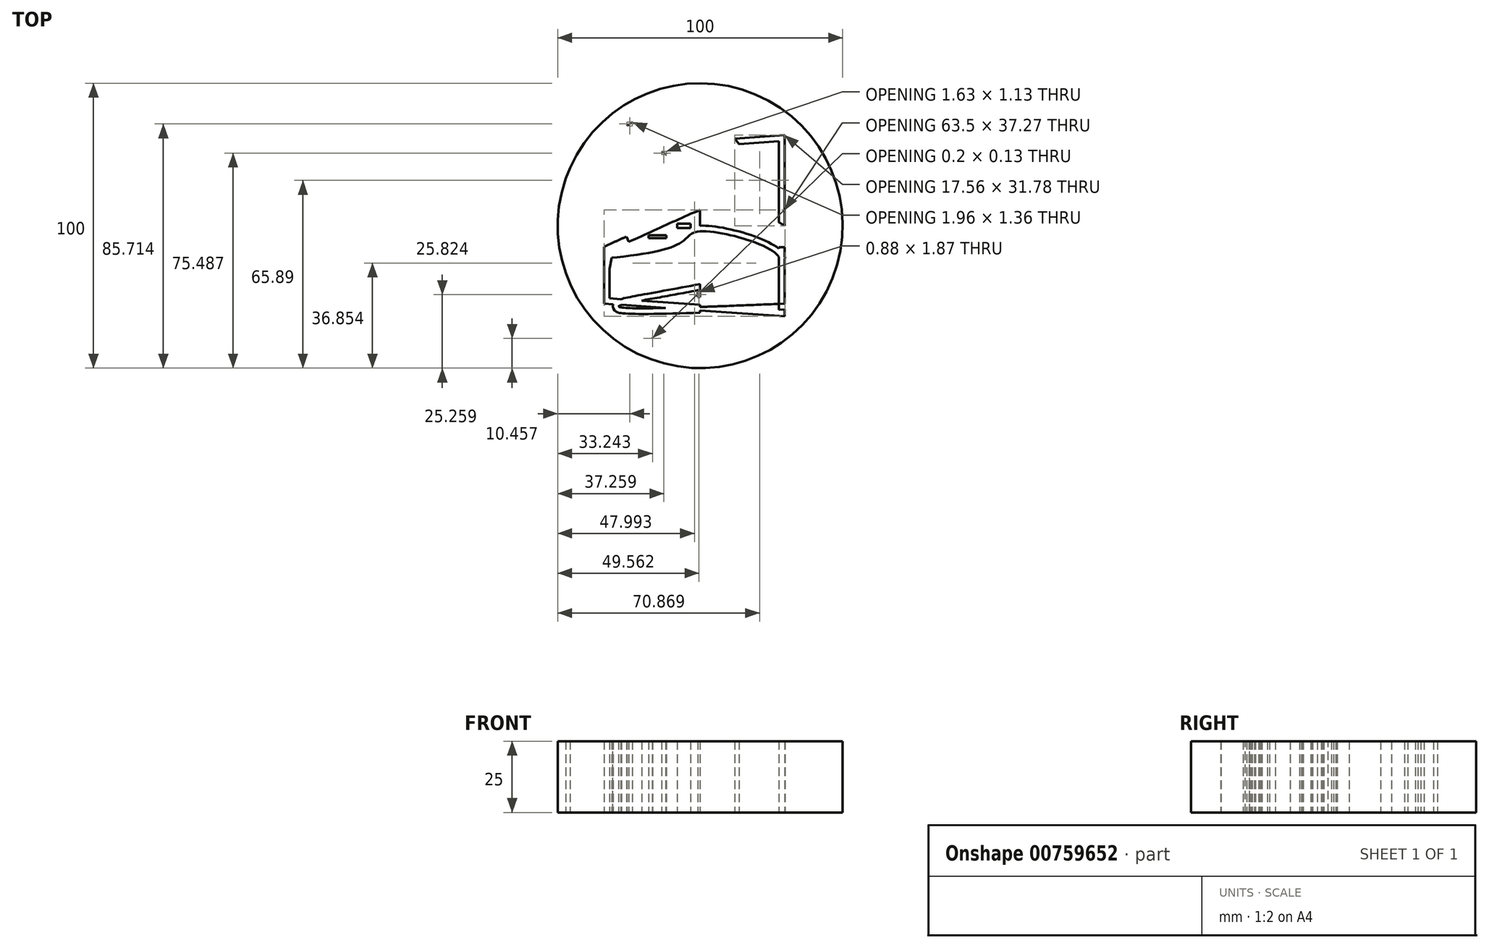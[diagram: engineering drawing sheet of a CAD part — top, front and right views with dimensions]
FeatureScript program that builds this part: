
annotation { "Feature Type Name" : "Feature", "Feature Type Description" : "" }
export const myFeature = defineFeature(function(context is Context, id is Id, definition is map)
    precondition{}
    {
        {
            var Q0;
            Q0=qCreatedBy(makeId("Top.planeOp"),FACE);
            var sketch = newSketch(context, id + "F0", { "sketchPlane" : qUnion([Q0])});
            skArc(sketch, "E0", {"start": v(33.76, -27.38) * mm, "mid": v(43.36, 3.01) * mm, "end": v(29.65, 31.78) * mm});
            skLineSegment(sketch, "E1", {"start": v(-33.76, 26.15) * mm, "end": v(-33.76, -27.38) * mm});
            skLineSegment(sketch, "E2", {"start": v(29.65, 31.78) * mm, "end": v(29.65, -3.54) * mm});
            skLineSegment(sketch, "E3", {"start": v(29.65, -27.38) * mm, "end": v(29.65, -31.78) * mm});
            skLineSegment(sketch, "E4", {"start": v(-29.02, 27.7) * mm, "end": v(-18.04, 28.47) * mm});
            skLineSegment(sketch, "E5", {"start": v(-33.76, -27.38) * mm, "end": v(29.65, -31.78) * mm});
            skLineSegment(sketch, "E6", {"start": v(0, 29.72) * mm, "end": v(0, -31.78) * mm});
            skArc(sketch, "E7", {"start": v(-9.95, 7.98) * mm, "mid": v(-7.68, 17.83) * mm, "end": v(-13.55, 26.05) * mm});
            skArc(sketch, "E8.0", {"start": v(-42.91, 16.74) * mm, "mid": v(-23.86, -39.18) * mm, "end": v(34.58, -30.54) * mm});
            skFitSpline(sketch, "E9.trimOffspring", {"points": [v(-33.76, -9.55) * mm, v(-8.04, -4.35) * mm, v(0, 0) * mm, v(29.65, -11.89) * mm, v(-27.62, -27.8) * mm, v(29.65, -27.38) * mm], "startDerivative": vector(179.63, 19.42) * mm, "endDerivative": vector(370.43, 15.15) * mm});
            skLineSegment(sketch, "E10.bottom", {"start": v(14.73, -23.24) * mm, "end": v(-0.88, -23.24) * mm});
            skLineSegment(sketch, "E10.top", {"start": v(14.73, -25.11) * mm, "end": v(-0.88, -25.11) * mm});
            skLineSegment(sketch, "E10.left", {"start": v(14.73, -23.24) * mm, "end": v(14.73, -25.11) * mm});
            skLineSegment(sketch, "E10.right", {"start": v(-0.88, -23.24) * mm, "end": v(-0.88, -25.11) * mm});
            skPoint(sketch, "E10.middle", {"position": v(6.93, -24.18) * mm});
            skLineSegment(sketch, "E11.bottom", {"start": v(27.65, -23.66) * mm, "end": v(20.84, -23.66) * mm});
            skLineSegment(sketch, "E11.top", {"start": v(27.65, -21.37) * mm, "end": v(20.84, -21.37) * mm});
            skLineSegment(sketch, "E11.left", {"start": v(29.65, -23.66) * mm, "end": v(29.65, -21.37) * mm});
            skLineSegment(sketch, "E11.right", {"start": v(20.84, -23.66) * mm, "end": v(20.84, -21.37) * mm});
            skPoint(sketch, "E11.middle", {"position": v(25.25, -22.51) * mm});
            skLineSegment(sketch, "E12.bottom", {"start": v(-11.85, -4.36) * mm, "end": v(-18.03, -4.36) * mm});
            skLineSegment(sketch, "E12.top", {"start": v(-11.85, -3.37) * mm, "end": v(-18.03, -3.37) * mm});
            skLineSegment(sketch, "E12.left", {"start": v(-11.85, -4.36) * mm, "end": v(-11.85, -3.37) * mm});
            skLineSegment(sketch, "E12.right", {"start": v(-18.03, -4.36) * mm, "end": v(-18.03, -3.37) * mm});
            skPoint(sketch, "E12.middle", {"position": v(-14.94, -3.87) * mm});
            skLineSegment(sketch, "E13.bottom", {"start": v(-3.33, -0.76) * mm, "end": v(-8.09, -0.76) * mm});
            skLineSegment(sketch, "E13.top", {"start": v(-3.33, 0.76) * mm, "end": v(-8.09, 0.76) * mm});
            skLineSegment(sketch, "E13.left", {"start": v(-3.33, -0.76) * mm, "end": v(-3.33, 0.76) * mm});
            skLineSegment(sketch, "E13.right", {"start": v(-8.09, -0.76) * mm, "end": v(-8.09, 0.76) * mm});
            skPoint(sketch, "E13.middle", {"position": v(-5.7, 0) * mm});
            skLineSegment(sketch, "E14.bottom", {"start": v(17.1, 2.32) * mm, "end": v(3, 2.32) * mm});
            skLineSegment(sketch, "E14.top", {"start": v(17.1, 4.3) * mm, "end": v(3, 4.3) * mm});
            skLineSegment(sketch, "E14.left", {"start": v(17.1, 2.32) * mm, "end": v(17.1, 4.3) * mm});
            skLineSegment(sketch, "E14.right", {"start": v(3, 2.32) * mm, "end": v(3, 4.3) * mm});
            skPoint(sketch, "E14.middle", {"position": v(10.04, 3.3) * mm});
            skLineSegment(sketch, "E15.left", {"start": v(29.65, -3.37) * mm, "end": v(29.65, -1.9) * mm});
            skPoint(sketch, "E15.middle", {"position": v(25.25, -2.64) * mm});
            skLineSegment(sketch, "E16.0", {"start": v(-28.89, 25.71) * mm, "end": v(-26.2, 25.9) * mm});
            skArc(sketch, "E17", {"start": v(-47.2, 16.53) * mm, "mid": v(46.48, -18.43) * mm, "end": v(-45.7, 20.3) * mm});
            skLineSegment(sketch, "E18.0", {"start": v(-31.76, 18.09) * mm, "end": v(-31.76, 13.5) * mm});
            skLineSegment(sketch, "E19.0", {"start": v(-31.76, -25.51) * mm, "end": v(27.65, -29.64) * mm});
            skLineSegment(sketch, "E20.0", {"start": v(27.65, 31.78) * mm, "end": v(27.65, 31.64) * mm});
            skArc(sketch, "E21.trimOffspring", {"start": v(37.17, -27.38) * mm, "mid": v(24.36, 39.52) * mm, "end": v(-41.13, 20.79) * mm});
            skLineSegment(sketch, "E22.trimOffspring", {"start": v(29.65, -7.53) * mm, "end": v(29.65, -27.38) * mm});
            skLineSegment(sketch, "E23.trimOffspring", {"start": v(27.65, -7.53) * mm, "end": v(27.65, -27.38) * mm});
            skLineSegment(sketch, "E24.left", {"start": v(-27.84, -8.9) * mm, "end": v(-27.84, -8.9) * mm});
            skFitSpline(sketch, "E25.trimOffspring", {"points": [v(-33.76, -9.55) * mm, v(-9.87, 1.2) * mm, v(11.16, 7.64) * mm, v(29.65, 0) * mm], "startDerivative": vector(67.01, 29.77) * mm, "endDerivative": vector(57.9, -35.17) * mm});
            skFitSpline(sketch, "E26.trimOffspring", {"points": [v(-33.76, -9.55) * mm, v(-8.04, -4.35) * mm, v(0, 0) * mm, v(29.65, -11.89) * mm, v(-27.62, -27.8) * mm, v(29.65, -27.38) * mm], "startDerivative": vector(179.63, 19.42) * mm, "endDerivative": vector(370.43, 15.15) * mm});
            skArc(sketch, "E27.0", {"start": v(-11.54, 9.19) * mm, "mid": v(-27.29, 22.44) * mm, "end": v(-12.93, 7.7) * mm});
            skLineSegment(sketch, "E28", {"start": v(23.18, 36.76) * mm, "end": v(27.65, 31.78) * mm});
            skLineSegment(sketch, "E29", {"start": v(-18.04, 28.47) * mm, "end": v(-23.17, 35.57) * mm});
            skLineSegment(sketch, "E30", {"start": v(-16.66, -39.48) * mm, "end": v(0, -31.78) * mm});
            skLineSegment(sketch, "E31", {"start": v(0, -31.78) * mm, "end": v(10.47, -33.17) * mm});
            skLineSegment(sketch, "E32", {"start": v(10.47, -33.17) * mm, "end": v(29.65, -31.78) * mm});
            skLineSegment(sketch, "E33", {"start": v(29.65, 28.51) * mm, "end": v(41.96, 1.31) * mm});
            skLineSegment(sketch, "E34", {"start": v(43.42, -1.9) * mm, "end": v(38.27, -11.44) * mm});
            skLineSegment(sketch, "E35", {"start": v(-33.76, 26.15) * mm, "end": v(-31.76, 13.5) * mm});
            skLineSegment(sketch, "E36", {"start": v(-31.76, -15.21) * mm, "end": v(-29.32, -1.9) * mm});
            skLineSegment(sketch, "E37.top", {"start": v(35.24, -15.12) * mm, "end": v(36.28, -15.12) * mm});
            skLineSegment(sketch, "E38.trimOffspring", {"start": v(36.28, -15.12) * mm, "end": v(29.65, -27.38) * mm});
            skLineSegment(sketch, "E39.0", {"start": v(29.65, 32.22) * mm, "end": v(29.65, -3.54) * mm});
            skLineSegment(sketch, "E39.2", {"start": v(22.96, 36.9) * mm, "end": v(23.03, 36.96) * mm});
            skLineSegment(sketch, "E39.6", {"start": v(-16.86, -39.6) * mm, "end": v(-1.76, -33.56) * mm});
            skLineSegment(sketch, "E40.0", {"start": v(10.61, -35.17) * mm, "end": v(27.11, -33.97) * mm});
            skLineSegment(sketch, "E41.0", {"start": v(30.93, 30.54) * mm, "end": v(43.35, 3.1) * mm});
            skLineSegment(sketch, "E42", {"start": v(-12.93, 7.7) * mm, "end": v(-11.61, 6.2) * mm});
            skLineSegment(sketch, "E43", {"start": v(-11.54, 9.19) * mm, "end": v(-9.95, 7.98) * mm});
            skLineSegment(sketch, "E44", {"start": v(33.76, -27.38) * mm, "end": v(37.17, -27.38) * mm});
            skLineSegment(sketch, "E45", {"start": v(31.85, -29.57) * mm, "end": v(34.58, -30.54) * mm});
            skPoint(sketch, "E46.orphan", {"position": v(-16.66, 26.56) * mm});
            skLineSegment(sketch, "E47.trimOffspring", {"start": v(-13.3, 28.8) * mm, "end": v(-11.92, 28.9) * mm});
            skPoint(sketch, "E48.orphan", {"position": v(28.88, 29.72) * mm});
            skArc(sketch, "E49.trimOffspring", {"start": v(22.96, 36.9) * mm, "mid": v(-1.67, 43.43) * mm, "end": v(-25.72, 35.03) * mm});
            skLineSegment(sketch, "E50", {"start": v(-47.2, 16.53) * mm, "end": v(-45.7, 20.3) * mm});
            skLineSegment(sketch, "E51.trimOffspring", {"start": v(27.65, -1.9) * mm, "end": v(20.85, -1.9) * mm});
            skFitSpline(sketch, "E52.0", {"points": [v(-34.57, -7.72) * mm, v(-31.78, -6.48) * mm, v(-27.59, -4.62) * mm, v(-22.03, -2.13) * mm, v(-17.87, -0.26) * mm, v(-14.42, 1.31) * mm, v(-11.67, 2.57) * mm, v(-8.93, 3.84) * mm, v(-5.5, 5.43) * mm, v(-1.34, 7.18) * mm, v(2.14, 8.37) * mm, v(4.94, 9.07) * mm, v(7.05, 9.45) * mm, v(8.82, 9.63) * mm, v(10.23, 9.67) * mm, v(11.65, 9.63) * mm, v(13.41, 9.46) * mm, v(15.47, 9.05) * mm, v(17.49, 8.47) * mm, v(20.12, 7.5) * mm, v(23.32, 6) * mm, v(27.05, 3.92) * mm, v(29.48, 2.44) * mm, v(30.69, 1.7) * mm]});
            skFitSpline(sketch, "E53.0", {"points": [v(-33.54, -11.54) * mm, v(-31.67, -11.33) * mm, v(-27.92, -10.93) * mm, v(-22.46, -10.26) * mm, v(-18.2, -9.6) * mm, v(-15.07, -8.96) * mm, v(-12.87, -8.43) * mm, v(-10.84, -7.82) * mm, v(-9.3, -7.24) * mm, v(-8.18, -6.72) * mm, v(-7.38, -6.3) * mm, v(-6.63, -5.82) * mm, v(-5.97, -5.34) * mm, v(-5.4, -4.86) * mm, v(-4.71, -4.25) * mm, v(-3.99, -3.58) * mm, v(-3.22, -2.96) * mm, v(-2.43, -2.51) * mm, v(-1.56, -2.22) * mm, v(-0.62, -2.05) * mm, v(0.5, -1.95) * mm, v(2.33, -1.98) * mm, v(5, -2.25) * mm, v(8.01, -2.74) * mm, v(11.2, -3.44) * mm, v(14.46, -4.3) * mm, v(17.64, -5.32) * mm, v(20.62, -6.44) * mm, v(23.28, -7.65) * mm, v(25.1, -8.68) * mm, v(26.23, -9.48) * mm, v(26.91, -10.05) * mm, v(27.39, -10.56) * mm, v(27.66, -10.97) * mm, v(27.74, -11.2) * mm, v(27.74, -11.26) * mm, v(27.74, -11.29) * mm, v(27.73, -11.32) * mm, v(27.69, -11.41) * mm, v(27.57, -11.6) * mm, v(27.27, -11.94) * mm, v(26.66, -12.44) * mm, v(25.8, -13) * mm, v(24.39, -13.76) * mm, v(22.13, -14.74) * mm, v(18.8, -15.9) * mm, v(14.98, -17.02) * mm, v(10.8, -18.1) * mm, v(6.34, -19.13) * mm, v(1.74, -20.1) * mm, v(-2.9, -21.03) * mm, v(-7.48, -21.9) * mm, v(-11.9, -22.7) * mm, v(-16.02, -23.44) * mm, v(-19.15, -24) * mm, v(-21.41, -24.41) * mm, v(-22.98, -24.7) * mm, v(-24.4, -24.99) * mm, v(-25.66, -25.25) * mm, v(-26.58, -25.46) * mm, v(-27.23, -25.62) * mm, v(-27.68, -25.73) * mm, v(-28.09, -25.85) * mm, v(-28.46, -25.97) * mm, v(-28.81, -26.1) * mm, v(-29.14, -26.24) * mm, v(-29.44, -26.4) * mm, v(-29.7, -26.58) * mm, v(-29.93, -26.78) * mm, v(-30.19, -27.06) * mm, v(-30.45, -27.5) * mm, v(-30.6, -28.03) * mm, v(-30.6, -28.52) * mm, v(-30.52, -28.99) * mm, v(-30.28, -29.49) * mm, v(-29.96, -29.87) * mm, v(-29.66, -30.1) * mm, v(-29.41, -30.26) * mm, v(-29.2, -30.36) * mm, v(-28.94, -30.46) * mm, v(-28.65, -30.54) * mm, v(-28.31, -30.62) * mm, v(-27.96, -30.68) * mm, v(-27.6, -30.73) * mm, v(-27.2, -30.77) * mm, v(-26.76, -30.81) * mm, v(-26.14, -30.86) * mm, v(-25.28, -30.9) * mm, v(-24.11, -30.94) * mm, v(-22.8, -30.97) * mm, v(-21.35, -30.99) * mm, v(-19.25, -30.99) * mm, v(-16.32, -30.96) * mm, v(-12.34, -30.89) * mm, v(-7.97, -30.78) * mm, v(-3.24, -30.64) * mm, v(1.8, -30.47) * mm, v(8.84, -30.21) * mm, v(18.15, -29.85) * mm, v(25.87, -29.53) * mm, v(29.73, -29.38) * mm]});
            skLineSegment(sketch, "E54", {"start": v(27.65, -27.38) * mm, "end": v(27.65, -29.58) * mm});
            skPoint(sketch, "E54.endSnap0", {"position": v(29.65, -29.58) * mm});
            skLineSegment(sketch, "E55", {"start": v(27.65, -29.58) * mm, "end": v(27.65, -29.64) * mm});
            skLineSegment(sketch, "E56.0", {"start": v(41.66, -0.96) * mm, "end": v(36.47, -10.55) * mm});
            skLineSegment(sketch, "E57", {"start": v(41.66, -0.96) * mm, "end": v(41.96, 1.31) * mm});
            skLineSegment(sketch, "E58", {"start": v(-33.62, -25.38) * mm, "end": v(-33.76, -25.38) * mm});
            skArc(sketch, "E59.trimOffspring", {"start": v(-32.8, -28.5) * mm, "mid": v(-0.71, -43.46) * mm, "end": v(31.85, -29.57) * mm});
            skLineSegment(sketch, "E60", {"start": v(36.47, -10.55) * mm, "end": v(38.27, -11.44) * mm});
            skLineSegment(sketch, "E61", {"start": v(29.65, -22.51) * mm, "end": v(35.24, -15.12) * mm});
            skLineSegment(sketch, "E62", {"start": v(-25.9, -3.86) * mm, "end": v(-25.08, -5.69) * mm});
            skLineSegment(sketch, "E63", {"start": v(-23.2, -8.4) * mm, "end": v(-23.33, -10.35) * mm});
            skLineSegment(sketch, "E64.0", {"start": v(-15.8, 30.44) * mm, "end": v(-14.4, 32.3) * mm});
            skLineSegment(sketch, "E65.0", {"start": v(-3.37, 43.33) * mm, "end": v(11.04, 33.3) * mm});
            skLineSegment(sketch, "E66.0", {"start": v(-16.38, 30.85) * mm, "end": v(-23.17, 35.57) * mm});
            skArc(sketch, "E67.trimOffspring", {"start": v(-23.76, 36.4) * mm, "mid": v(-32.37, 29) * mm, "end": v(-38.77, 19.65) * mm});
            skLineSegment(sketch, "E68", {"start": v(-23.76, 36.4) * mm, "end": v(-25.72, 35.03) * mm});
            skLineSegment(sketch, "E69", {"start": v(-16.38, 30.85) * mm, "end": v(-15.8, 30.44) * mm});
            skPoint(sketch, "E70.end.orphan", {"position": v(-16.57, 28.62) * mm});
            skLineSegment(sketch, "E71.0", {"start": v(-13.3, 28.8) * mm, "end": v(-3.89, 41.25) * mm});
            skPoint(sketch, "E72.end.orphan", {"position": v(14.63, 30.82) * mm});
            skPoint(sketch, "E73.start.orphan", {"position": v(15.8, 30.82) * mm});
            skLineSegment(sketch, "E74.trimOffspring", {"start": v(27.65, 29.64) * mm, "end": v(27.65, -1.9) * mm});
            skArc(sketch, "E75.trimOffspring", {"start": v(-31.47, 11.7) * mm, "mid": v(-23.03, 3.57) * mm, "end": v(-11.61, 6.2) * mm});
            skLineSegment(sketch, "E76.trimOffspring", {"start": v(-24.05, 36.19) * mm, "end": v(-24.06, 36.2) * mm});
            skFitSpline(sketch, "E77.trimOffspring", {"points": [v(-34.57, -7.72) * mm, v(-31.78, -6.48) * mm, v(-27.59, -4.62) * mm, v(-22.03, -2.13) * mm, v(-17.87, -0.26) * mm, v(-14.42, 1.31) * mm, v(-11.67, 2.57) * mm, v(-8.93, 3.84) * mm, v(-5.5, 5.43) * mm, v(-1.34, 7.18) * mm, v(2.14, 8.37) * mm, v(4.94, 9.07) * mm, v(7.05, 9.45) * mm, v(8.82, 9.63) * mm, v(10.23, 9.67) * mm, v(11.65, 9.63) * mm, v(13.41, 9.46) * mm, v(15.47, 9.05) * mm, v(17.49, 8.47) * mm, v(20.12, 7.5) * mm, v(23.32, 6) * mm, v(27.05, 3.92) * mm, v(29.48, 2.44) * mm, v(30.69, 1.7) * mm]});
            skLineSegment(sketch, "E78", {"start": v(12.09, 30.56) * mm, "end": v(29.65, 31.78) * mm});
            skLineSegment(sketch, "E79", {"start": v(13.65, 28.66) * mm, "end": v(27.65, 29.64) * mm});
            skLineSegment(sketch, "E80", {"start": v(10.57, 30.46) * mm, "end": v(11.46, 28.51) * mm});
            skLineSegment(sketch, "E81", {"start": v(12.09, 30.56) * mm, "end": v(13.65, 28.66) * mm});
            skFitSpline(sketch, "E82", {"points": [v(7.45, 25.37) * mm, v(13.65, 21.57) * mm, v(9.2, 15.55) * mm, v(17.63, 20.1) * mm, v(7.45, 25.37) * mm]});
            skLineSegment(sketch, "E83", {"start": v(-28.89, 25.71) * mm, "end": v(-29.02, 27.7) * mm});
            skArc(sketch, "E84.trimOffspring", {"start": v(-26.2, 25.9) * mm, "mid": v(-29.77, 22.56) * mm, "end": v(-31.76, 18.09) * mm});
            skLineSegment(sketch, "E85.trimOffspring", {"start": v(-14.8, 26.69) * mm, "end": v(-14.5, 26.71) * mm});
            skLineSegment(sketch, "E86.0", {"start": v(-14.5, 26.71) * mm, "end": v(-11.93, 24.92) * mm});
            skLineSegment(sketch, "E87", {"start": v(-3.89, 41.25) * mm, "end": v(6.76, 33.3) * mm});
            skPoint(sketch, "E88.center.orphan", {"position": v(10.96, 29.72) * mm});
            skLineSegment(sketch, "E89.trimOffspring", {"start": v(-1.76, -33.56) * mm, "end": v(10.2, -35.15) * mm});
            skLineSegment(sketch, "E90.trimOffspring", {"start": v(-11, 26.95) * mm, "end": v(11.46, 28.51) * mm});
            skLineSegment(sketch, "E91", {"start": v(-26.2, 25.9) * mm, "end": v(-14.8, 26.69) * mm});
            skPoint(sketch, "E92.orphan", {"position": v(-15.93, 28.62) * mm});
            skLineSegment(sketch, "E93.trimOffspring", {"start": v(-31.76, -15.21) * mm, "end": v(-31.76, -25.51) * mm});
            skLineSegment(sketch, "E94.trimOffspring", {"start": v(-31.47, 11.7) * mm, "end": v(-29.32, -1.9) * mm});
            skLineSegment(sketch, "E95", {"start": v(10.61, -35.17) * mm, "end": v(10.2, -35.15) * mm});
            skLineSegment(sketch, "E96", {"start": v(-16.66, -39.48) * mm, "end": v(-16.86, -39.6) * mm});
            skFitSpline(sketch, "E97.trimOffspring", {"points": [v(-33.76, -9.55) * mm, v(-8.04, -4.35) * mm, v(0, 0) * mm, v(29.65, -11.89) * mm, v(-27.62, -27.8) * mm, v(29.65, -27.38) * mm], "startDerivative": vector(179.63, 19.42) * mm, "endDerivative": vector(370.43, 15.15) * mm});
            skLineSegment(sketch, "E98", {"start": v(-16.66, -39.48) * mm, "end": v(-17.24, -39.9) * mm});
            skLineSegment(sketch, "E99", {"start": v(-41.13, 15.86) * mm, "end": v(-42.91, 16.74) * mm});
            skLineSegment(sketch, "E100", {"start": v(-41.13, 15.86) * mm, "end": v(-40.59, 15.55) * mm});
            skPoint(sketch, "E15.bottom.end.orphan", {"position": v(20.85, -3.37) * mm});
            skLineSegment(sketch, "E101", {"start": v(20.85, -1.9) * mm, "end": v(20.85, -2.92) * mm});
            skLineSegment(sketch, "E102", {"start": v(20.85, -2.92) * mm, "end": v(27.65, -2.92) * mm});
            skLineSegment(sketch, "E103.trimOffspring", {"start": v(27.65, -2.92) * mm, "end": v(27.65, -3.54) * mm});
            skLineSegment(sketch, "E104.top", {"start": v(27.65, -7.53) * mm, "end": v(29.65, -7.53) * mm});
            skLineSegment(sketch, "E105.bottom", {"start": v(27.65, -3.54) * mm, "end": v(29.65, -3.54) * mm});
            skLineSegment(sketch, "E106.trimOffspring", {"start": v(29.65, -4.5) * mm, "end": v(29.65, -4.5) * mm});
            skLineSegment(sketch, "E107.left", {"start": v(-17.39, 26.5) * mm, "end": v(-17.39, 26.2) * mm});
            skLineSegment(sketch, "E107.right", {"start": v(-11.92, 29.25) * mm, "end": v(-11.92, 28.9) * mm});
            skLineSegment(sketch, "E108.trimOffspring", {"start": v(0, 29.72) * mm, "end": v(10.57, 30.46) * mm});
            skLineSegment(sketch, "E109.left", {"start": v(6.56, 32.45) * mm, "end": v(6.56, 32.45) * mm});
            skLineSegment(sketch, "E109.right", {"start": v(7.46, 32.45) * mm, "end": v(7.46, 32.45) * mm});
            skLineSegment(sketch, "E110.bottom", {"start": v(6.76, 33.3) * mm, "end": v(11.04, 33.3) * mm});
            skPoint(sketch, "E111.start.orphan", {"position": v(-45.3, 15.86) * mm});
            skLineSegment(sketch, "E112", {"start": v(-41.13, 20.79) * mm, "end": v(-38.9, 19.72) * mm});
            skArc(sketch, "E113.trimOffspring", {"start": v(-40.59, 15.55) * mm, "mid": v(-42.92, -6.83) * mm, "end": v(-33.76, -27.38) * mm});
            skLineSegment(sketch, "E114", {"start": v(-38.9, 19.72) * mm, "end": v(-38.77, 19.65) * mm});
            skLineSegment(sketch, "E115.trimOffspring", {"start": v(-13.41, 33.6) * mm, "end": v(-6.3, 43) * mm});
            skLineSegment(sketch, "E116", {"start": v(-31.76, 13.5) * mm, "end": v(-31.43, 11.46) * mm});
            skLineSegment(sketch, "E117.trimOffspring", {"start": v(-13.3, 28.8) * mm, "end": v(-4.32, 29.42) * mm});
            skSolve(sketch);
        }
        {
            var Q0;
            {var subQ5=sQuery(id+"F0.wireOp",EDGE,"E18.0");Q0=makeQuery(id+"F0.imprint","IMPRINT",FACE,{"disambiguationData":[TD([[makeQuery(id+"F0.imprint","IMPRINT",EDGE,{"derivedFrom":subQ5}),1.0]])]});}
            var Q1;
            {var subQ9=sQuery(id+"F0.wireOp",EDGE,"E35");Q1=makeQuery(id+"F0.imprint","IMPRINT",FACE,{"disambiguationData":[TD([[makeQuery(id+"F0.imprint","IMPRINT",EDGE,{"derivedFrom":subQ9}),-1.0]])]});}
            var Q2;
            Q2=makeQuery(id+"F0.imprint","IMPRINT",FACE,{"disambiguationData":[TD([[makeQuery(id+"F0.imprint","IMPRINT",EDGE,{"derivedFrom":sQuery(id+"F0.wireOp",EDGE,"E8.0")}),1.0]])]});
            var Q3;
            {var subQ6=sQuery(id+"F0.wireOp",EDGE,"E40.0");Q3=makeQuery(id+"F0.imprint","IMPRINT",FACE,{"disambiguationData":[TD([[makeQuery(id+"F0.imprint","IMPRINT",EDGE,{"derivedFrom":subQ6}),-1.0]])]});}
            var Q4;
            {var subQ4=sQuery(id+"F0.wireOp",EDGE,"E31");Q4=makeQuery(id+"F0.imprint","IMPRINT",FACE,{"disambiguationData":[TD([[makeQuery(id+"F0.imprint","IMPRINT",EDGE,{"derivedFrom":subQ4}),1.0]])]});}
            var Q5;
            {var subQ7=sQuery(id+"F0.wireOp",EDGE,"E30");Q5=makeQuery(id+"F0.imprint","IMPRINT",FACE,{"disambiguationData":[TD([[makeQuery(id+"F0.imprint","IMPRINT",EDGE,{"derivedFrom":subQ7}),-1.0]])]});}
            var Q6;
            {var subQ6=sQuery(id+"F0.wireOp",EDGE,"E10.left");Q6=makeQuery(id+"F0.imprint","IMPRINT",FACE,{"disambiguationData":[TD([[makeQuery(id+"F0.imprint","IMPRINT",EDGE,{"derivedFrom":subQ6}),1.0]])]});}
            var Q7;
            {var subQ5=sQuery(id+"F0.wireOp",EDGE,"E10.left");Q7=makeQuery(id+"F0.imprint","IMPRINT",FACE,{"disambiguationData":[TD([[makeQuery(id+"F0.imprint","IMPRINT",EDGE,{"derivedFrom":subQ5}),-1.0]])]});}
            var Q8;
            {var subQ0=sQuery(id+"F0.wireOp",EDGE,"E11.bottom");Q8=makeQuery(id+"F0.imprint","IMPRINT",FACE,{"disambiguationData":[TD([[makeQuery(id+"F0.imprint","IMPRINT",EDGE,{"derivedFrom":subQ0}),-1.0]])]});}
            var Q9;
            {var subQ6=sQuery(id+"F0.wireOp",EDGE,"E3");Q9=makeQuery(id+"F0.imprint","IMPRINT",FACE,{"disambiguationData":[TD([[makeQuery(id+"F0.imprint","IMPRINT",EDGE,{"derivedFrom":subQ6}),-1.0]])]});}
            var Q10;
            {var subQ0=sQuery(id+"F0.wireOp",EDGE,"E10.right");Q10=makeQuery(id+"F0.imprint","IMPRINT",FACE,{"disambiguationData":[TD([[makeQuery(id+"F0.imprint","IMPRINT",EDGE,{"derivedFrom":subQ0}),-1.0]])]});}
            var Q11;
            {var subQ0=sQuery(id+"F0.wireOp",EDGE,"E53.0");var subQ1=sQuery(id+"F0.wireOp",EDGE,"E6");var subQ2=makeQuery(id+"F0.imprint","INTERSECT",VERTEX,{"disambiguationData":[OD(1.0)],"derivedFrom":[subQ1,subQ0]});Q11=makeQuery(id+"F0.imprint","IMPRINT",FACE,{"disambiguationData":[TD([[makeQuery(id+"F0.imprint","IMPRINT",EDGE,{"disambiguationData":[TD([[subQ2,-1.0]])],"derivedFrom":subQ1}),-1.0]])]});}
            var Q12;
            {var subQ0=sQuery(id+"F0.wireOp",EDGE,"E53.0");var subQ1=sQuery(id+"F0.wireOp",EDGE,"E6");var subQ2=makeQuery(id+"F0.imprint","INTERSECT",VERTEX,{"disambiguationData":[OD(0.0)],"derivedFrom":[subQ1,subQ0]});Q12=makeQuery(id+"F0.imprint","IMPRINT",FACE,{"disambiguationData":[TD([[makeQuery(id+"F0.imprint","IMPRINT",EDGE,{"disambiguationData":[TD([[subQ2,-1.0]])],"derivedFrom":subQ1}),1.0]])]});}
            var Q13;
            {var subQ0=sQuery(id+"F0.wireOp",EDGE,"E53.0");var subQ1=sQuery(id+"F0.wireOp",EDGE,"E6");var subQ2=makeQuery(id+"F0.imprint","INTERSECT",VERTEX,{"disambiguationData":[OD(1.0)],"derivedFrom":[subQ1,subQ0]});Q13=makeQuery(id+"F0.imprint","IMPRINT",FACE,{"disambiguationData":[TD([[makeQuery(id+"F0.imprint","IMPRINT",EDGE,{"disambiguationData":[TD([[subQ2,-1.0]])],"derivedFrom":subQ1}),1.0]])]});}
            var Q14;
            Q14=makeQuery(id+"F0.imprint","IMPRINT",FACE,{"disambiguationData":[TD([[makeQuery(id+"F0.imprint","IMPRINT",EDGE,{"derivedFrom":sQuery(id+"F0.wireOp",EDGE,"E37.top")}),-1.0]])]});
            var Q15;
            {var subQ9=sQuery(id+"F0.wireOp",EDGE,"E9.trimOffspring");Q15=makeQuery(id+"F0.imprint","IMPRINT",FACE,{"disambiguationData":[TD([[makeQuery(id+"F0.imprint","IMPRINT",EDGE,{"derivedFrom":subQ9}),1.0]])]});}
            var Q16;
            {var subQ5=sQuery(id+"F0.wireOp",EDGE,"E51.trimOffspring");Q16=makeQuery(id+"F0.imprint","IMPRINT",FACE,{"disambiguationData":[TD([[makeQuery(id+"F0.imprint","IMPRINT",EDGE,{"derivedFrom":subQ5}),1.0]])]});}
            var Q17;
            {var subQ5=sQuery(id+"F0.wireOp",EDGE,"E33");Q17=makeQuery(id+"F0.imprint","IMPRINT",FACE,{"disambiguationData":[TD([[makeQuery(id+"F0.imprint","IMPRINT",EDGE,{"derivedFrom":subQ5}),1.0]])]});}
            var Q18;
            {var subQ0=sQuery(id+"F0.wireOp",EDGE,"E41.0");Q18=makeQuery(id+"F0.imprint","IMPRINT",FACE,{"disambiguationData":[TD([[makeQuery(id+"F0.imprint","IMPRINT",EDGE,{"derivedFrom":subQ0}),1.0]])]});}
            var Q19;
            {var subQ0=sQuery(id+"F0.wireOp",EDGE,"E25.trimOffspring");var subQ1=sQuery(id+"F0.wireOp",EDGE,"E6");var subQ2=makeQuery(id+"F0.imprint","INTERSECT",VERTEX,{"derivedFrom":[subQ1,subQ0]});Q19=makeQuery(id+"F0.imprint","IMPRINT",FACE,{"disambiguationData":[TD([[makeQuery(id+"F0.imprint","IMPRINT",EDGE,{"disambiguationData":[TD([[subQ2,1.0]])],"derivedFrom":subQ1}),1.0]])]});}
            var Q20;
            Q20=makeQuery(id+"F0.imprint","IMPRINT",FACE,{"disambiguationData":[TD([[makeQuery(id+"F0.imprint","IMPRINT",EDGE,{"derivedFrom":sQuery(id+"F0.wireOp",EDGE,"E82")}),1.0]])]});
            var Q21;
            {var subQ4=sQuery(id+"F0.wireOp",EDGE,"E80");Q21=makeQuery(id+"F0.imprint","IMPRINT",FACE,{"disambiguationData":[TD([[makeQuery(id+"F0.imprint","IMPRINT",EDGE,{"derivedFrom":subQ4}),-1.0]])]});}
            var Q22;
            {var subQ0=sQuery(id+"F0.wireOp",EDGE,"E26.trimOffspring");var subQ1=sQuery(id+"F0.wireOp",EDGE,"E6");var subQ2=makeQuery(id+"F0.imprint","INTERSECT",VERTEX,{"derivedFrom":[subQ1,subQ0]});Q22=makeQuery(id+"F0.imprint","IMPRINT",FACE,{"disambiguationData":[TD([[makeQuery(id+"F0.imprint","IMPRINT",EDGE,{"disambiguationData":[TD([[subQ2,-1.0]])],"derivedFrom":subQ1}),1.0]])]});}
            var Q23;
            {var subQ5=sQuery(id+"F0.wireOp",EDGE,"E62");Q23=makeQuery(id+"F0.imprint","IMPRINT",FACE,{"disambiguationData":[TD([[makeQuery(id+"F0.imprint","IMPRINT",EDGE,{"derivedFrom":subQ5}),1.0]])]});}
            var Q24;
            Q24=makeQuery(id+"F0.imprint","IMPRINT",FACE,{"disambiguationData":[TD([[makeQuery(id+"F0.imprint","IMPRINT",EDGE,{"derivedFrom":sQuery(id+"F0.wireOp",EDGE,"E14.bottom")}),-1.0]])]});
            var Q25;
            {var subQ62=sQuery(id+"F0.wireOp",EDGE,"E3");Q25=makeQuery(id+"F0.imprint","IMPRINT",FACE,{"disambiguationData":[TD([[makeQuery(id+"F0.imprint","IMPRINT",EDGE,{"derivedFrom":subQ62}),1.0]])]});}
            var Q26;
            Q26=makeQuery(id+"F0.imprint","IMPRINT",FACE,{"disambiguationData":[TD([[makeQuery(id+"F0.imprint","IMPRINT",EDGE,{"derivedFrom":sQuery(id+"F0.wireOp",EDGE,"E13.bottom")}),-1.0]])]});
            var Q27;
            Q27=makeQuery(id+"F0.imprint","IMPRINT",FACE,{"disambiguationData":[TD([[makeQuery(id+"F0.imprint","IMPRINT",EDGE,{"derivedFrom":sQuery(id+"F0.wireOp",EDGE,"E12.bottom")}),-1.0]])]});
            extrude(context, id + "F1", {"entities" : qUnion([Q0, Q1, Q2, Q3, Q4, Q5, Q6, Q7, Q8, Q9, Q10, Q11, Q12, Q13, Q14, Q15, Q16, Q17, Q18, Q19, Q20, Q21, Q22, Q23, Q24, Q25, Q26, Q27]), "depth" : 25 * mm, "offsetDistance" : 25 * mm});
        }
    });
